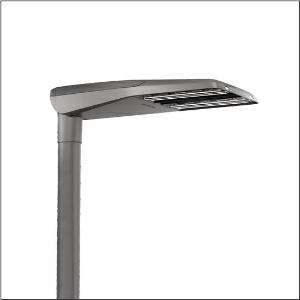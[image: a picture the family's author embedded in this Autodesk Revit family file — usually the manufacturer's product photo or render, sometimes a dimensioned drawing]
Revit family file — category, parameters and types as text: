
# Revit family: streetlight_sl_11_iq_midi___st1_2a_5xc3a11f08me_159a
name_source: partatom
category: Lighting Fixtures
units: mm (PartAtom-declared; Revit-internal decimal feet)

## family parameters
Cut with Voids When Loaded = No
Host = Face
Light Source = No
Part Type = Normal
Room Calculation Point = No
Round Connector Dimension = Use Diameter
Shared = No

## types (1)
- --- (1 x LED, 11170 lm, 124.5 W, 1800K)
    Apparent Load = 125 VA
    CIE Flux Codes = 32 70 96 100 100
    Color Rendering = 70
    Color Temperature = 1800K
    Default Elevation = 1800 mm  [stored 5.90551 ft]
    Description = Streetlight SL 11 iQ midi, mast luminaire, primary light control with 3 zone facetted reflector, of plastic, silver coated, highly specular, primary optical cover: cover, of PMMA, transparent, light distribution: ST1.2a, light emission: direct distribution, primary light characteristic: asymmetric, installation type: post-top, side-entry, LED, High Power LED, rated luminous flux: 11.170lm, luminous efficacy: 90lm/W, light colour: 718, colour temperature: 1800K, control: Street-Remote, Auto-Match, Temp-Guard, Lumen-Switch, Night-Set, Smart-Wire, Light-Fading, Desk-Remote (wireless, voltage-free reading and setting of iQ features in the workshop via application-optimized NFC function/RFID function), optimised constant luminous flux control (CLO 2.0), with cable H07RN-F 5x 1.5mm², mains connection: 230..240V, AC, 50/60Hz, connection cable pre-assembled, cable length: 12,5m, start of lifetime: 125W, end of service life: 132W, reduction: 55W, luminaire housing, of diecast aluminium, powder-coated, Siteco® metallic grey (DB 702S), please order mast flange separately, inclination adjustable without tools: 0°, 5°, 10°, 15° (post-top) | 0°, -5°, -10°, -15° (side-entry), sealing non-destructively replaceable, multi-level sealing system, length: 780mm, width: 376mm, height: 118mm, mast flange for spigot size: 42mm (side-entry): 5XC10008XM4, 60/48mm (side-entry/post-top): 5XC10108XM2, 76/60mm (side-entry/post-top): 5XC10108XM1, equipment: Power, protection rating (complete): IP66, insulation class (complete): insulation class II (safety insulation), certification: CE, ENEC, VDE, impact resistance: IK09, permissible operating ambient temperature for outdoor applications: -25..+50°C, standard-compliant lighting for roads and squares, Environmental Product Declaration (EPD) tested and certified by an independent institute, packaging unit: 1 piece

Light Distribution: ST1.2a
    Height = 118 mm
    Lamp = 1 x LED
    Lamp Light Flux = 11170 lm
    Lamp Power = 124.5 W
    Lamp count = 1
    Length = 780 mm
    Luminous efficacy = 90 lm/W
    Manufacturer = Siteco
    ModVariant = No
    Model = 5XC3A11F08ME
    Number of Poles = 1
    OnlyDefault = Yes
    Power Factor = 1
    Product Name = Streetlight SL 11 iQ midi | ST1.2a
    Product group = mast luminaire | pylon top
    ProductGroupID = 6100
    Protection Class = Protection class II
    Protection Degree = IP 66
    RLX_Detail_Level = 1
    RLX_Emergency_Light_Flux = 0 lm
    RLX_Emergency_Type = 0
    RLX_Emergency_Type_DB = No
    RlxData = <blob elided: 70765 chars, md5=30b3dc0c>
    Socket = socket
    Standby Power = 0 W
    System Light Flux = 11170 lm
    System Power = 125 W
    Type Comments = factory setting: luminous flux: 100 % | dim-lin: 254 | 554 mA
    Type Image = l_1005960.jpg
    URL = http://relux.com
    VarID = @adj_029405
    Voltage = 0 V
    Weight = 0.00 kg
    Width = 376 mm

note: [stored X ft] marks values corroborated as IEEE doubles in the binary element streams (Revit-internal decimal feet)

## geometry (parser evidence)
native form markers: Blend x4, Sweep x9
no freeform markers — native parametric forms only
